# Revit family: Move
name_source: partatom
category: Furniture
revit_build: Autodesk Revit 2015 (Build: 20140606_1530(x64)
units: mm (PartAtom-declared; Revit-internal decimal feet)

## types (4) — shared parameters
Manufacturer = Isku Oy
Table top thickness = 25 mm  [stored 0.082021 ft]
Type Comments = Available as antimicrobial
URL = www.isku.fi

## per-type parameters (varying)
| type | Leg material | Table top depth | Table top material | Table top width | Wheel material |
| Move A16 | <By Category> | 800 mm | <By Category> | 1600 mm  [stored 5.24934 ft] | <By Category> |
| Move A18 | <By Category> | 800 mm | <By Category> | 1800 mm  [stored 5.90551 ft] | <By Category> |
| Move C16 | <By Category> | 700 mm  [stored 2.29659 ft] | <By Category> | 1600 mm  [stored 5.24934 ft] | <By Category> |
| Move C18 | Silver | 700 mm  [stored 2.29659 ft] | White Plywood | 1800 mm  [stored 5.90551 ft] | Rubber plastic |

note: [stored X ft] marks values corroborated as IEEE doubles in the binary element streams (Revit-internal decimal feet)

## geometry (parser evidence)
native form markers: Sweep x11
no freeform markers — native parametric forms only
